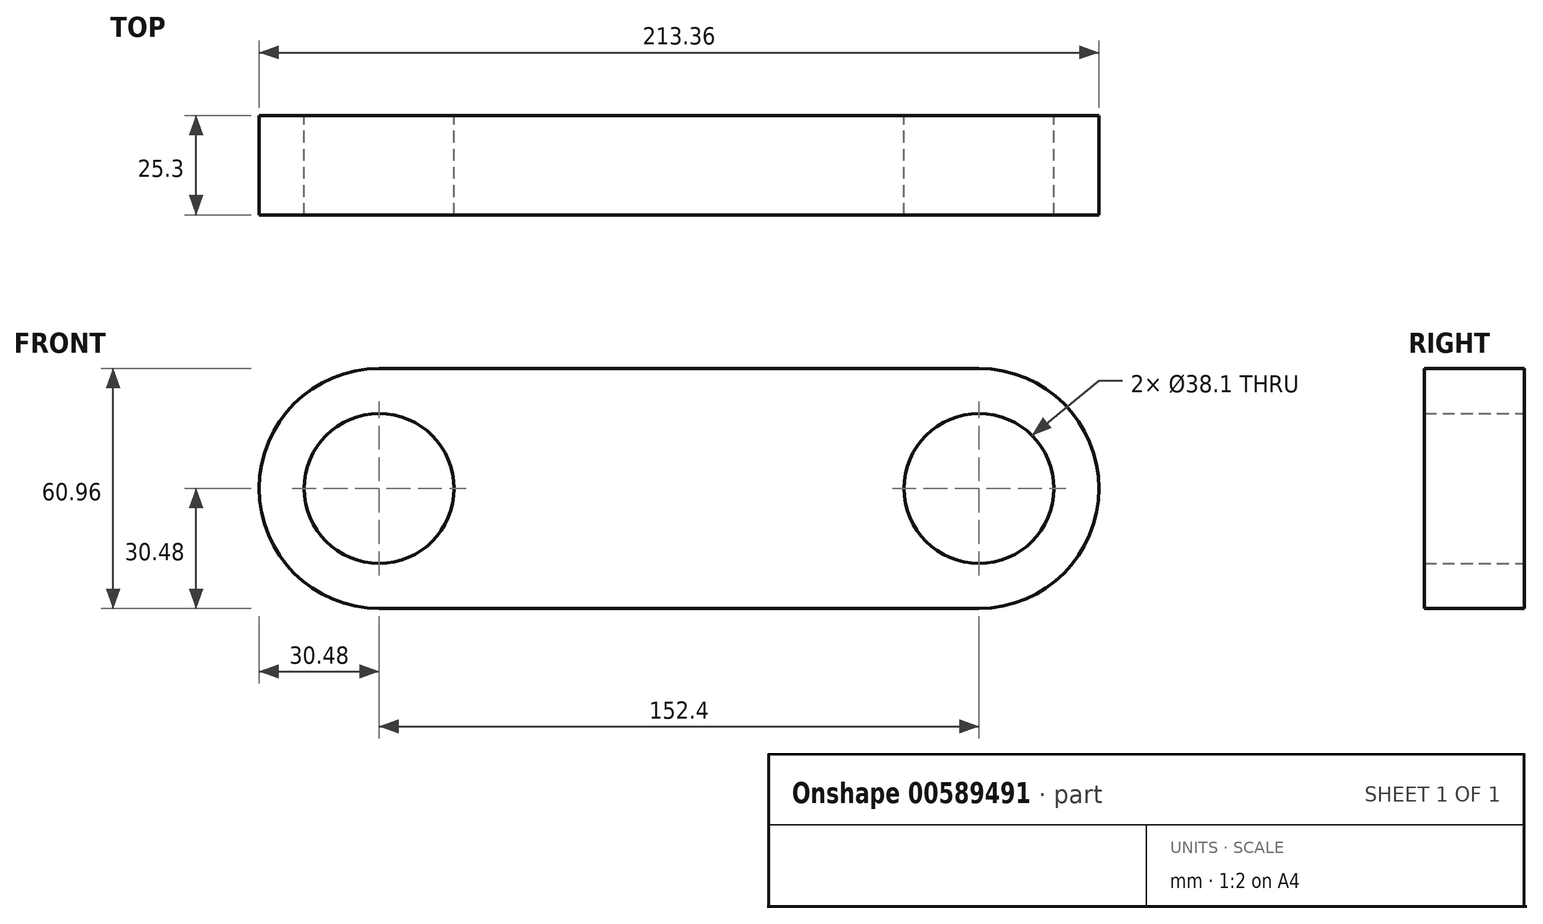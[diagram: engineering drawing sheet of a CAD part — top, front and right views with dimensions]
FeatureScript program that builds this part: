
annotation { "Feature Type Name" : "Feature", "Feature Type Description" : "" }
export const myFeature = defineFeature(function(context is Context, id is Id, definition is map)
    precondition{}
    {
        {
            var Q0;
            Q0=qCreatedBy(makeId("Front.planeOp"),FACE);
            var sketch = newSketch(context, id + "F0", { "sketchPlane" : qUnion([Q0])});
            skLineSegment(sketch, "E0.bottom", {"start": v(76.2, 30.48) * mm, "end": v(-76.2, 30.48) * mm});
            skLineSegment(sketch, "E0.top", {"start": v(76.2, -30.48) * mm, "end": v(-76.2, -30.48) * mm});
            skLineSegment(sketch, "E0.left", {"start": v(76.2, 30.48) * mm, "end": v(76.2, -30.48) * mm});
            skLineSegment(sketch, "E0.right", {"start": v(-76.2, 30.48) * mm, "end": v(-76.2, -30.48) * mm});
            skPoint(sketch, "E0.middle", {"position": v(0, 0) * mm});
            skCircle(sketch, "E1", {"center": v(76.2, 0) * mm, "radius": 30.48 * mm});
            skCircle(sketch, "E2", {"center": v(-76.2, 0) * mm, "radius": 30.48 * mm});
            skCircle(sketch, "E3", {"center": v(-76.2, 0) * mm, "radius": 19.05 * mm});
            skCircle(sketch, "E4", {"center": v(76.2, 0) * mm, "radius": 19.05 * mm});
            skSolve(sketch);
        }
        {
            var Q0;
            Q0 = qSketchRegion(id + "F0", true);
            extrude(context, id + "F1", {"entities" : qUnion([Q0]), "depth" : 25.3 * mm, "offsetDistance" : 30.48 * mm});
        }
    });
